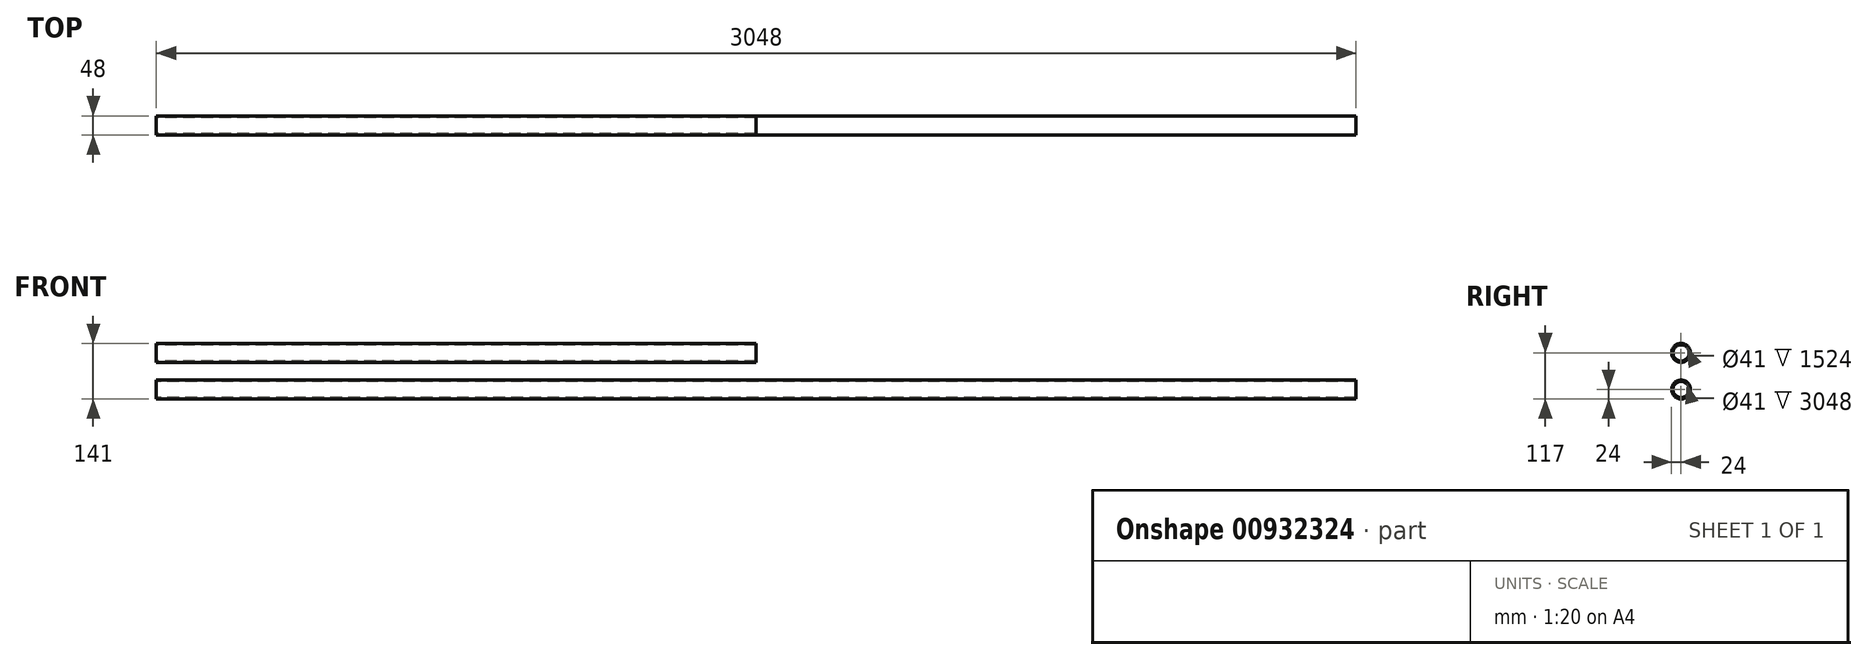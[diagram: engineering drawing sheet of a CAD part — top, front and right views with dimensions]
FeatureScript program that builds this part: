
annotation { "Feature Type Name" : "Feature", "Feature Type Description" : "" }
export const myFeature = defineFeature(function(context is Context, id is Id, definition is map)
    precondition{}
    {
        {
            var Q0;
            Q0=qCreatedBy(makeId("Right.planeOp"),FACE);
            var sketch = newSketch(context, id + "F0", { "sketchPlane" : qUnion([Q0])});
            skCircle(sketch, "E0", {"center": v(0, 0) * mm, "radius": 24 * mm});
            skCircle(sketch, "E1", {"center": v(0, 0) * mm, "radius": 20.5 * mm});
            skSolve(sketch);
        }
        {
            var Q0;
            Q0=makeQuery(id+"F0.imprint","IMPRINT",FACE,{"disambiguationData":[TD([[makeQuery(id+"F0.imprint","IMPRINT",EDGE,{"derivedFrom":sQuery(id+"F0.wireOp",EDGE,"E0")}),1.0]])]});
            extrude(context, id + "F1", {"entities" : qUnion([Q0]), "depth" : 3048 * mm, "offsetDistance" : 25 * mm});
        }
        {
            var Q0;
            Q0=qCreatedBy(makeId("Right.planeOp"),FACE);
            var sketch = newSketch(context, id + "F2", { "sketchPlane" : qUnion([Q0])});
            skCircle(sketch, "E2", {"center": v(0, 93) * mm, "radius": 24 * mm});
            skCircle(sketch, "E3", {"center": v(0, 93) * mm, "radius": 20.5 * mm});
            skSolve(sketch);
        }
        {
            var Q0;
            Q0=makeQuery(id+"F2.imprint","IMPRINT",FACE,{"disambiguationData":[TD([[makeQuery(id+"F2.imprint","IMPRINT",EDGE,{"derivedFrom":sQuery(id+"F2.wireOp",EDGE,"E2")}),1.0]])]});
            extrude(context, id + "F3", {"entities" : qUnion([Q0]), "depth" : 1524 * mm, "offsetDistance" : 25 * mm});
        }
    });
